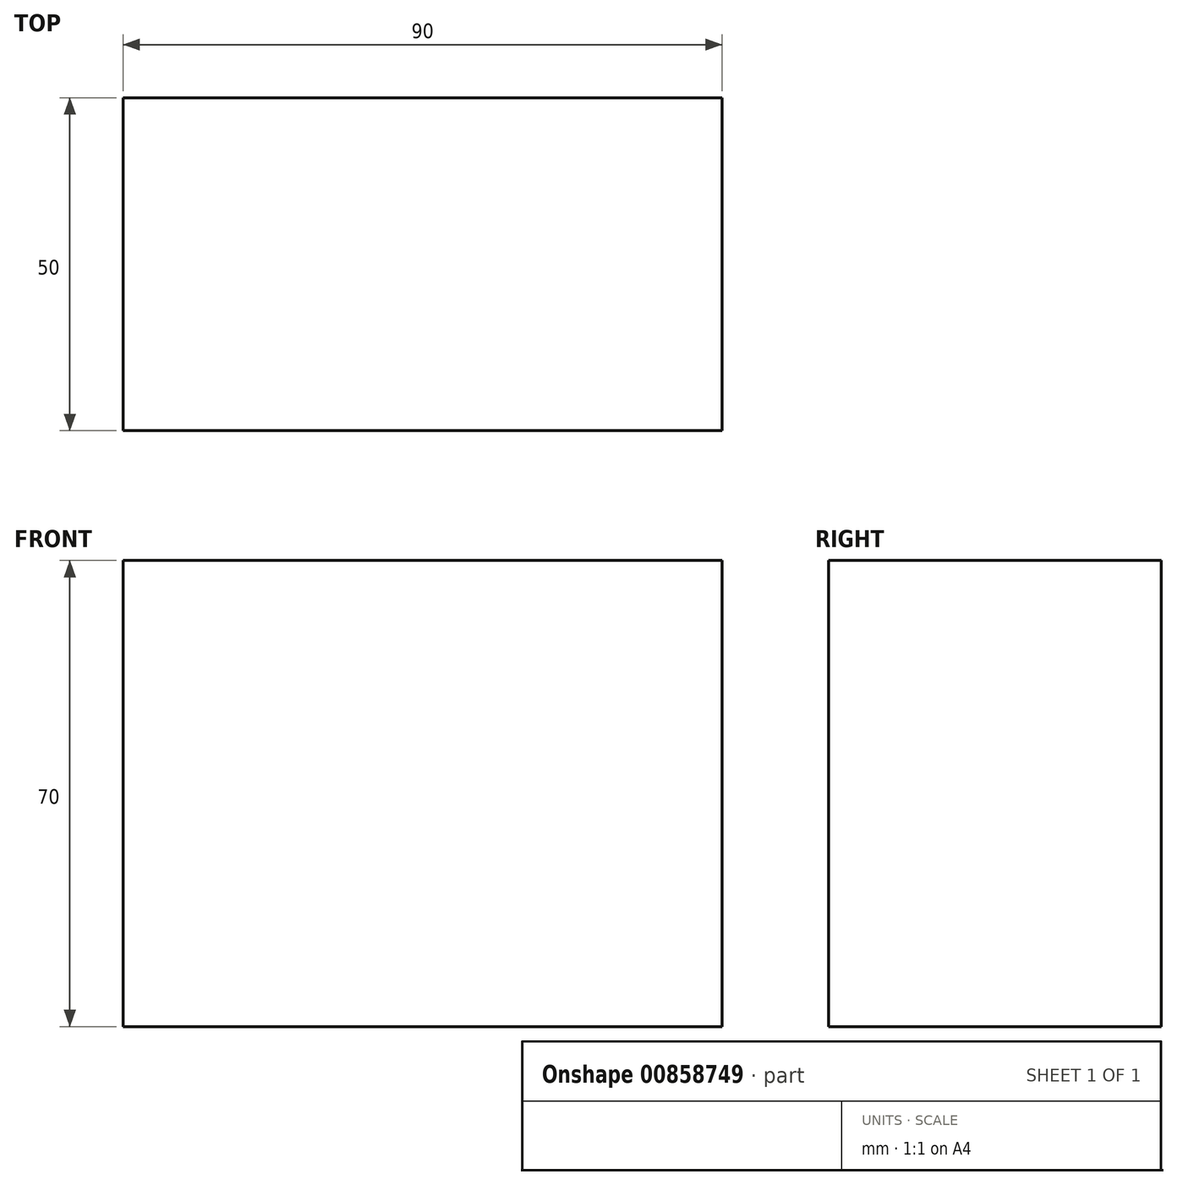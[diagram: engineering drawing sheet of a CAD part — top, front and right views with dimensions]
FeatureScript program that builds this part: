
annotation { "Feature Type Name" : "Feature", "Feature Type Description" : "" }
export const myFeature = defineFeature(function(context is Context, id is Id, definition is map)
    precondition{}
    {
        {
            var Q0;
            Q0=qCreatedBy(makeId("Top.planeOp"),FACE);
            var sketch = newSketch(context, id + "F0", { "sketchPlane" : qUnion([Q0])});
            skLineSegment(sketch, "E0.bottom", {"start": v(-45, 25) * mm, "end": v(45, 25) * mm});
            skLineSegment(sketch, "E0.top", {"start": v(-45, -25) * mm, "end": v(45, -25) * mm});
            skLineSegment(sketch, "E0.left", {"start": v(-45, 25) * mm, "end": v(-45, -25) * mm});
            skLineSegment(sketch, "E0.right", {"start": v(45, 25) * mm, "end": v(45, -25) * mm});
            skPoint(sketch, "E0.middle", {"position": v(0, 0) * mm});
            skSolve(sketch);
        }
        {
            var Q0;
            Q0 = qSketchRegion(id + "F0", true);
            extrude(context, id + "F1", {"entities" : qUnion([Q0]), "depth" : 70 * mm, "offsetDistance" : 25 * mm});
        }
    });
